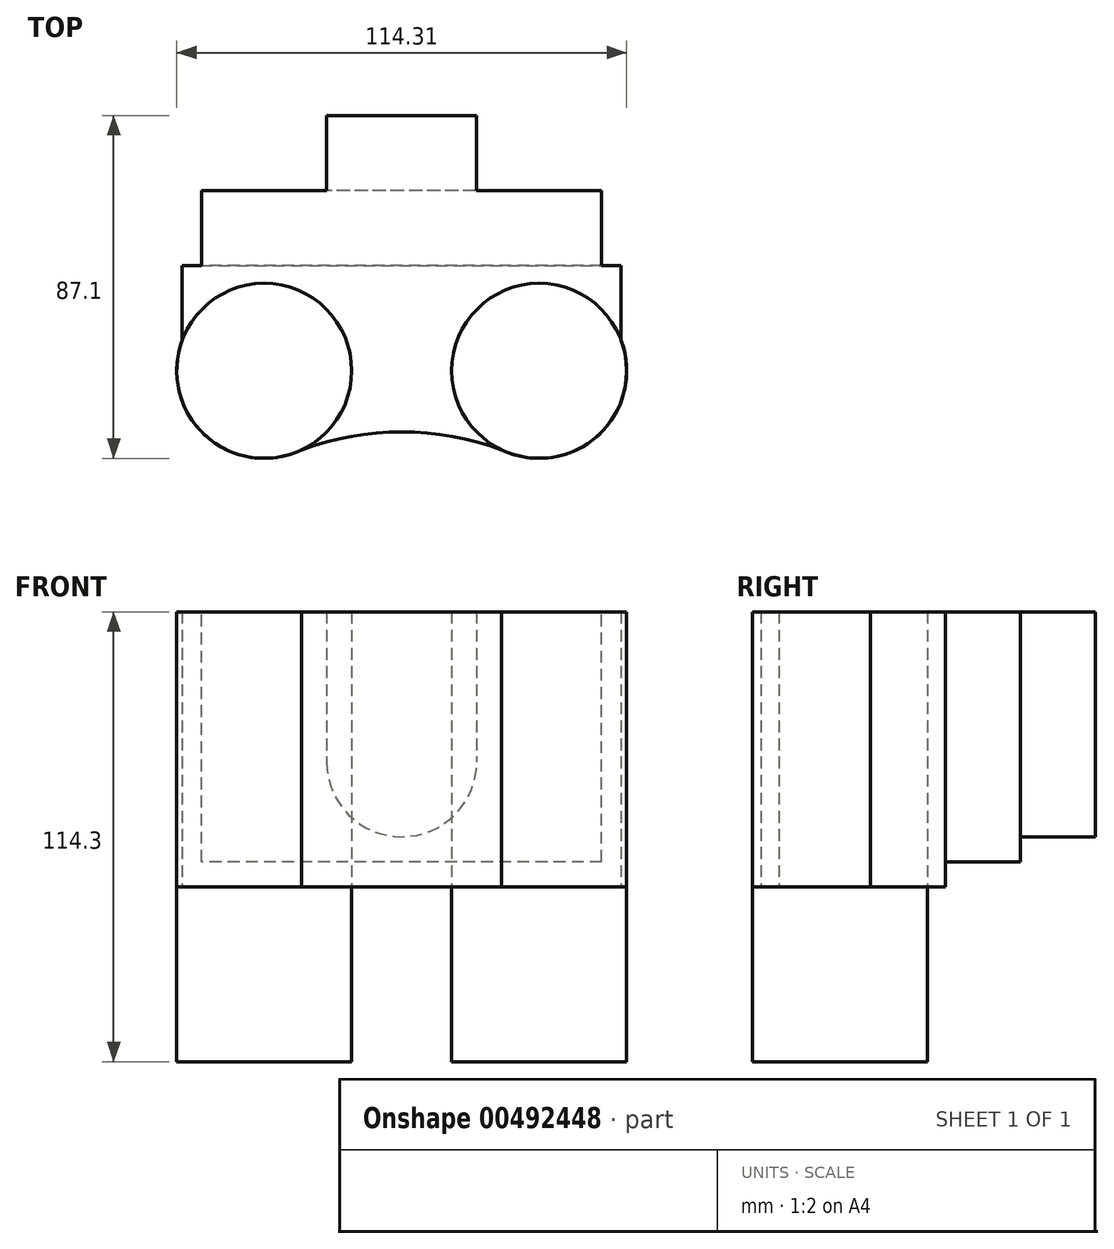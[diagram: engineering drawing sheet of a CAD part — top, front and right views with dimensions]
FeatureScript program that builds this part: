
annotation { "Feature Type Name" : "Feature", "Feature Type Description" : "" }
export const myFeature = defineFeature(function(context is Context, id is Id, definition is map)
    precondition{}
    {
        {
            var Q0;
            Q0=qCreatedBy(makeId("Top.planeOp"),FACE);
            var sketch = newSketch(context, id + "F0", { "sketchPlane" : qUnion([Q0])});
            skCircle(sketch, "E0", {"center": v(0, 0) * mm, "radius": 22.23 * mm});
            skCircle(sketch, "E1", {"center": v(69.85, 0) * mm, "radius": 22.23 * mm});
            skSolve(sketch);
        }
        {
            var Q0;
            Q0=makeQuery(id+"F0.imprint","IMPRINT",FACE,{"disambiguationData":[TD([[makeQuery(id+"F0.imprint","IMPRINT",EDGE,{"derivedFrom":sQuery(id+"F0.wireOp",EDGE,"E0")}),1.0]])]});
            var Q1;
            Q1=makeQuery(id+"F0.imprint","IMPRINT",FACE,{"disambiguationData":[TD([[makeQuery(id+"F0.imprint","IMPRINT",EDGE,{"derivedFrom":sQuery(id+"F0.wireOp",EDGE,"E1")}),1.0]])]});
            extrude(context, id + "F1", {"entities" : qUnion([Q0, Q1]), "depth" : 114.3 * mm});
        }
        {
            var Q0;
            Q0=qCreatedBy(makeId("Top.planeOp"),FACE);
            cPlane(context, id + "F2", {"entities" : qUnion([Q0]), "cplaneType" : CPlaneType.OFFSET, "offset" : 44.45 * mm, "width" : 152.4 * mm, "height" : 152.4 * mm});
        }
        {
            var Q0;
            Q0=qCreatedBy(id+"F2.planeOp",FACE);
            var sketch = newSketch(context, id + "F3", { "sketchPlane" : qUnion([Q0])});
            skCircle(sketch, "E2.0.0", {"center": v(0, 0) * mm, "radius": 22.23 * mm});
            skCircle(sketch, "E3.0.0", {"center": v(69.85, 0) * mm, "radius": 22.23 * mm});
            skLineSegment(sketch, "E4.bottom", {"start": v(-20.84, 7.72) * mm, "end": v(90.69, 7.72) * mm});
            skLineSegment(sketch, "E4.top", {"start": v(-20.84, 26.77) * mm, "end": v(90.69, 26.77) * mm});
            skLineSegment(sketch, "E4.left", {"start": v(-20.84, 7.72) * mm, "end": v(-20.84, 26.77) * mm});
            skLineSegment(sketch, "E4.right", {"start": v(90.69, 7.72) * mm, "end": v(90.69, 26.77) * mm});
            skArc(sketch, "E5", {"start": v(60.33, -20.08) * mm, "mid": v(34.92, -15.52) * mm, "end": v(9.53, -20.08) * mm});
            skSolve(sketch);
        }
        {
            var Q0;
            Q0 = qSketchRegion(id + "F3", true);
            var Q1;
            Q1=makeQuery(id+"F1.opExtrude","CAP_FACE",FACE,{"disambiguationData":[OSD([sQuery(id+"F0.wireOp",EDGE,"E0")])],"isStart":false});
            extrude(context, id + "F4", {"entities" : qUnion([Q0]), "endBound" : BoundingType.UP_TO_SURFACE, "endBoundEntityFace" : qUnion([Q1]), "depth" : 31.75 * mm});
        }
        {
            var Q0;
            Q0=makeQuery(id+"F4.opExtrude","SWEPT_FACE",FACE,{"disambiguationData":[OSD([sQuery(id+"F3.wireOp",EDGE,"E4.top")])]});
            var sketch = newSketch(context, id + "F5", { "sketchPlane" : qUnion([Q0])});
            skLineSegment(sketch, "E6.bottom", {"start": v(-85.73, 50.8) * mm, "end": v(15.88, 50.8) * mm});
            skLineSegment(sketch, "E6.top", {"start": v(-85.73, 114.3) * mm, "end": v(15.88, 114.3) * mm});
            skLineSegment(sketch, "E6.left", {"start": v(-85.73, 50.8) * mm, "end": v(-85.73, 114.3) * mm});
            skLineSegment(sketch, "E6.right", {"start": v(15.88, 50.8) * mm, "end": v(15.88, 114.3) * mm});
            skLineSegment(sketch, "E7.0.0", {"start": v(-90.69, 44.45) * mm, "end": v(20.84, 44.45) * mm});
            skLineSegment(sketch, "E7.0.1", {"start": v(20.84, 44.45) * mm, "end": v(20.84, 114.3) * mm});
            skLineSegment(sketch, "E7.0.2", {"start": v(20.84, 114.3) * mm, "end": v(-90.69, 114.3) * mm});
            skLineSegment(sketch, "E7.0.3", {"start": v(-90.69, 114.3) * mm, "end": v(-90.69, 44.45) * mm});
            skLineSegment(sketch, "E8", {"start": v(-34.92, 76.2) * mm, "end": v(-34.92, 44.45) * mm});
            skLineSegment(sketch, "E9", {"start": v(-34.92, 114.3) * mm, "end": v(-34.92, 50.8) * mm});
            skSolve(sketch);
        }
        {
            var Q0;
            {var subQ4=sQuery(id+"F5.wireOp",EDGE,"E6.left");Q0=makeQuery(id+"F5.imprint","IMPRINT",FACE,{"disambiguationData":[TD([[makeQuery(id+"F5.imprint","IMPRINT",EDGE,{"derivedFrom":subQ4}),-1.0]])]});}
            var Q1;
            {var subQ0=sQuery(id+"F5.wireOp",EDGE,"E6.right");Q1=makeQuery(id+"F5.imprint","IMPRINT",FACE,{"disambiguationData":[TD([[makeQuery(id+"F5.imprint","IMPRINT",EDGE,{"derivedFrom":subQ0}),1.0]])]});}
            var Q2;
            Q2=makeQuery(id+"F4.opExtrude","CAP_FACE",FACE,{"disambiguationData":[OSD([sQuery(id+"F0.wireOp",EDGE,"E0")])],"isStart":false});
            extrude(context, id + "F6", {"entities" : qUnion([Q0, Q1]), "operationType" : NewBodyOperationType.ADD, "endBoundEntityFace" : qUnion([Q2]), "depth" : 19.05 * mm});
        }
        {
            var Q0;
            Q0=makeQuery(id+"F6.opExtrude","CAP_FACE",FACE,{"disambiguationData":[OSD([sQuery(id+"F5.wireOp",EDGE,"E6.bottom"),sQuery(id+"F5.wireOp",EDGE,"E6.left"),sQuery(id+"F5.wireOp",EDGE,"E6.right"),sQuery(id+"F5.wireOp",EDGE,"E7.0.2")])],"isStart":false});
            var sketch = newSketch(context, id + "F7", { "sketchPlane" : qUnion([Q0])});
            skLineSegment(sketch, "E10.bottom", {"start": v(-53.97, 114.3) * mm, "end": v(-15.87, 114.3) * mm});
            skLineSegment(sketch, "E10.top", {"start": v(-53.97, 76.2) * mm, "end": v(-15.87, 76.2) * mm});
            skLineSegment(sketch, "E10.left", {"start": v(-53.97, 114.3) * mm, "end": v(-53.97, 76.2) * mm});
            skLineSegment(sketch, "E10.right", {"start": v(-15.87, 114.3) * mm, "end": v(-15.87, 76.2) * mm});
            skArc(sketch, "E11", {"start": v(-53.97, 76.2) * mm, "mid": v(-34.92, 57.15) * mm, "end": v(-15.87, 76.2) * mm});
            skSolve(sketch);
        }
        {
            var Q0;
            Q0=makeQuery(id+"F7.imprint","IMPRINT",FACE,{"disambiguationData":[TD([[makeQuery(id+"F7.imprint","IMPRINT",EDGE,{"derivedFrom":sQuery(id+"F7.wireOp",EDGE,"E10.bottom")}),1.0]])]});
            var Q1;
            Q1=makeQuery(id+"F7.imprint","IMPRINT",FACE,{"disambiguationData":[TD([[makeQuery(id+"F7.imprint","IMPRINT",EDGE,{"derivedFrom":sQuery(id+"F7.wireOp",EDGE,"E10.top")}),-1.0]])]});
            extrude(context, id + "F8", {"entities" : qUnion([Q0, Q1]), "operationType" : NewBodyOperationType.ADD, "depth" : 19.05 * mm});
        }
    });
